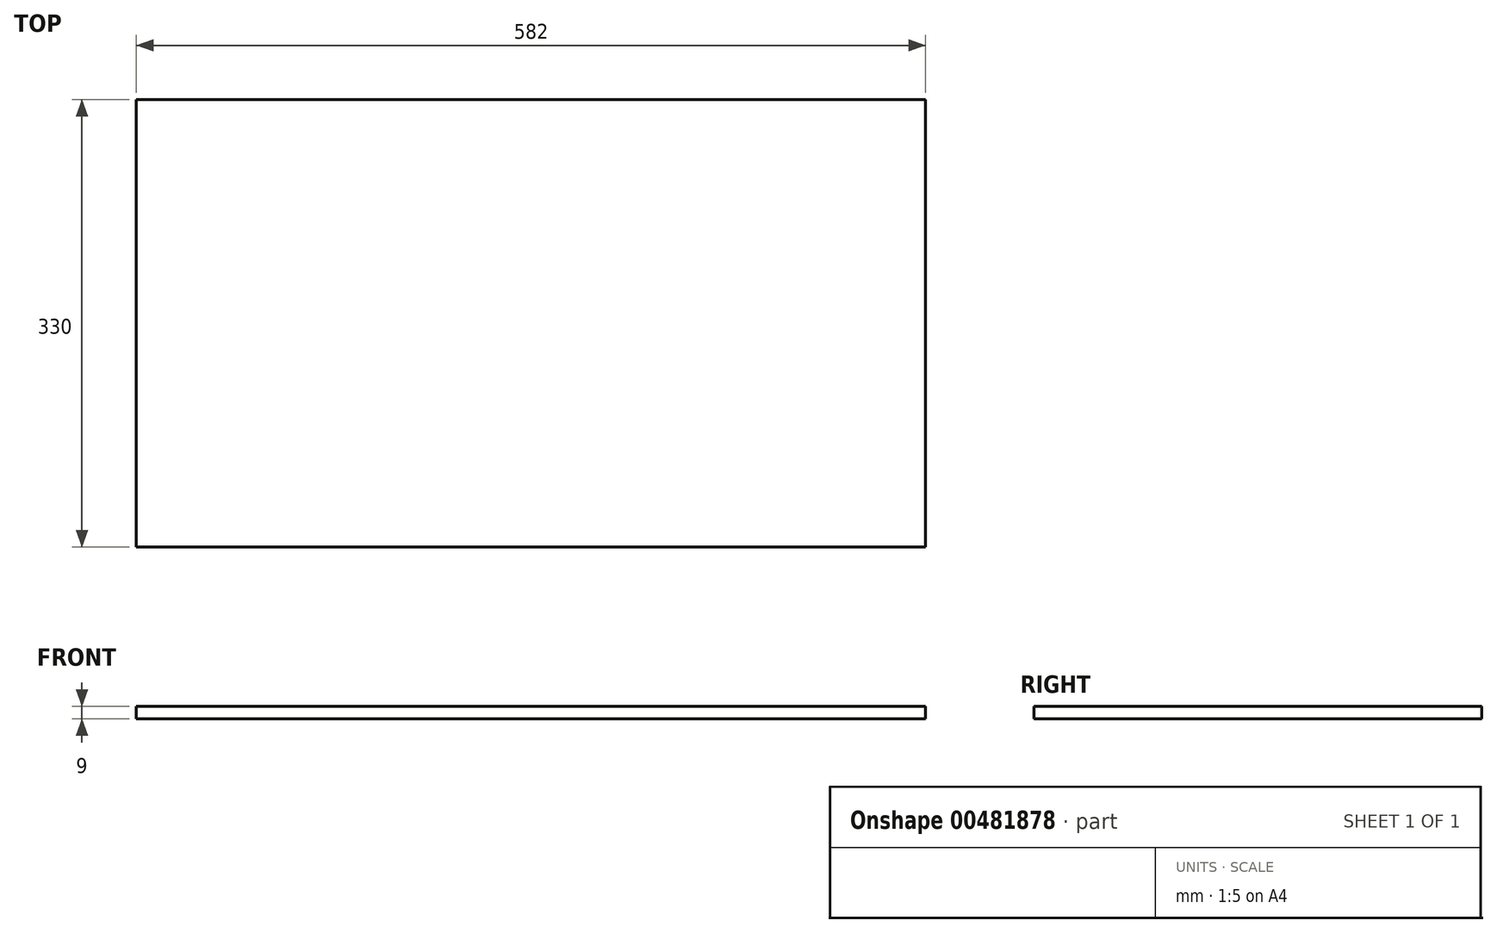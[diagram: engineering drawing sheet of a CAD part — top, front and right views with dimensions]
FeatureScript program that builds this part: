
annotation { "Feature Type Name" : "Feature", "Feature Type Description" : "" }
export const myFeature = defineFeature(function(context is Context, id is Id, definition is map)
    precondition{}
    {
        {
            var Q0;
            Q0=qCreatedBy(makeId("Top.planeOp"),FACE);
            var sketch = newSketch(context, id + "F0", { "sketchPlane" : qUnion([Q0])});
            skLineSegment(sketch, "E0.bottom", {"start": v(0, 0) * mm, "end": v(-582, 0) * mm});
            skLineSegment(sketch, "E0.top", {"start": v(0, 330) * mm, "end": v(-582, 330) * mm});
            skLineSegment(sketch, "E0.left", {"start": v(0, 0) * mm, "end": v(0, 330) * mm});
            skLineSegment(sketch, "E0.right", {"start": v(-582, 0) * mm, "end": v(-582, 330) * mm});
            skSolve(sketch);
        }
        {
            var Q0;
            Q0 = qSketchRegion(id + "F0", true);
            extrude(context, id + "F1", {"entities" : qUnion([Q0]), "depth" : 9 * mm});
        }
    });
